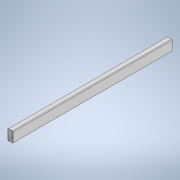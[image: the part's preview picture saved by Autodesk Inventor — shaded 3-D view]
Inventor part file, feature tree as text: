
AUTODESK INVENTOR PART (.ipt)
format: ipt  version: 2020 (Build 240168000, 168)  size: 127,488 bytes
history: native  units: in
note: dims shown in document units (in); Inventor stores cm internally (conversion verified against a paired STEP export)
features: extrude x1, sketch x1
ambient origin geometry x8: Origin, YZ Plane, XZ Plane, XY Plane, X Axis, Y Axis, Z Axis, Center Point
bodies: Solid1 (feature_tree)
feature tree (2):
  extrude  "Extrusion1"  Depth=1.0in
  sketch  "Sketch1"  dims[d0=2.0in d1=1.0in d2=0.125in d3=0.125in d4=0.125in d5=0.125in d6=0.125in d7=0.125in d8=0.125in d9=0.125in d10=0.125in d11=30.0in d12=0.0in]
